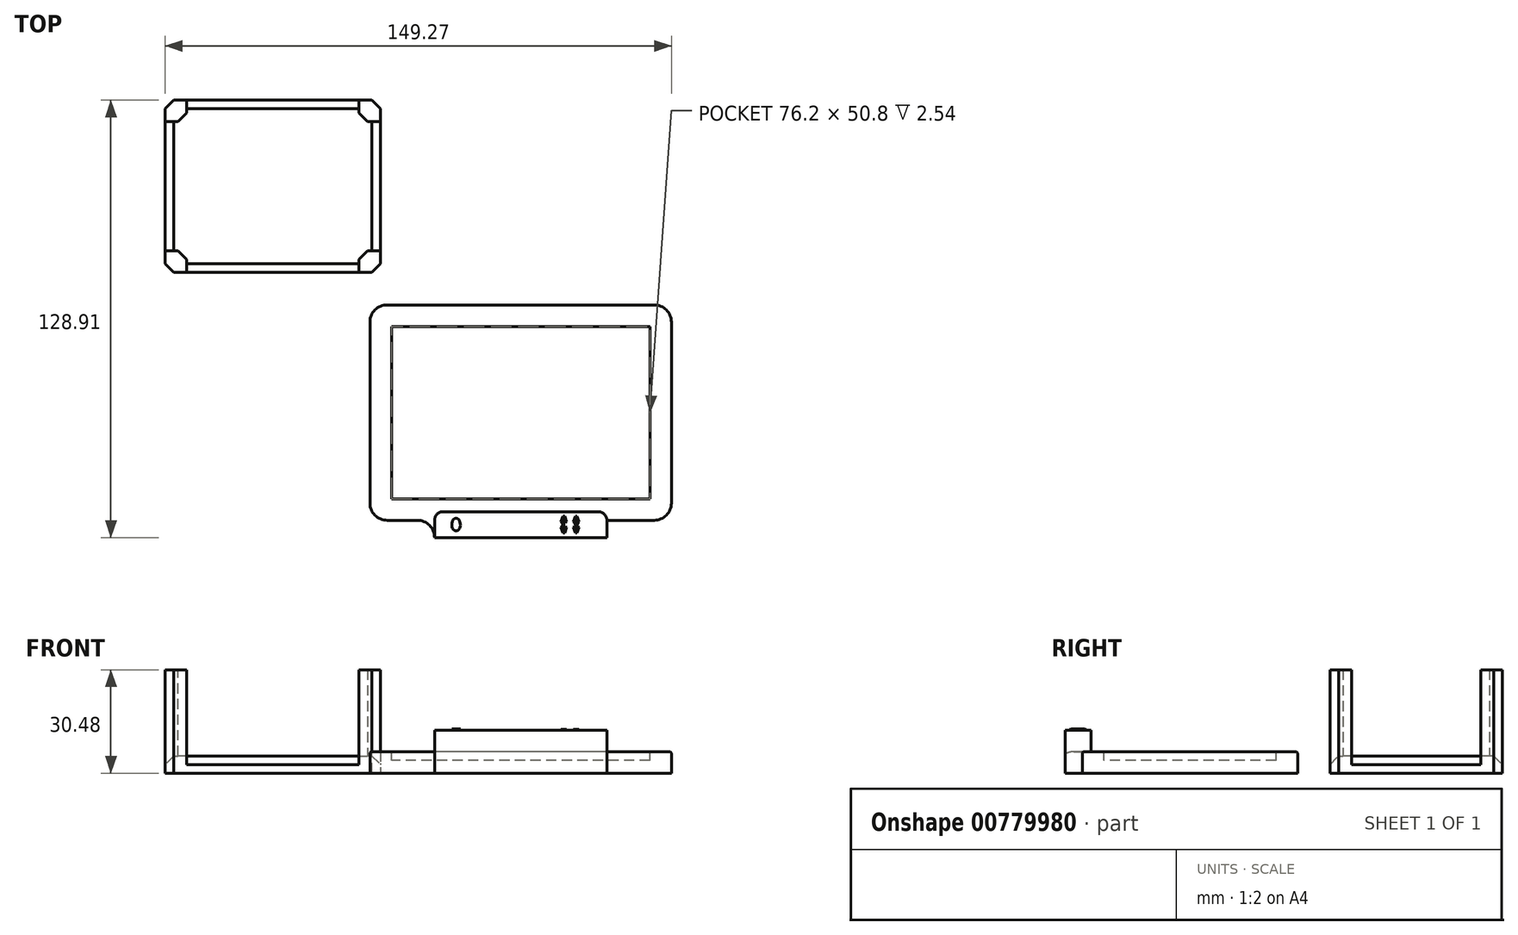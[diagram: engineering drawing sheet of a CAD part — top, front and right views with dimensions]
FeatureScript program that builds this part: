
annotation { "Feature Type Name" : "Feature", "Feature Type Description" : "" }
export const myFeature = defineFeature(function(context is Context, id is Id, definition is map)
    precondition{}
    {
        {
            var Q0;
            Q0=qCreatedBy(makeId("Top.planeOp"),FACE);
            var sketch = newSketch(context, id + "F0", { "sketchPlane" : qUnion([Q0])});
            skLineSegment(sketch, "E0.bottom", {"start": v(44.45, 31.75) * mm, "end": v(-44.45, 31.75) * mm});
            skLineSegment(sketch, "E0.top", {"start": v(44.45, -31.75) * mm, "end": v(-44.45, -31.75) * mm});
            skLineSegment(sketch, "E0.left", {"start": v(44.45, 31.75) * mm, "end": v(44.45, -31.75) * mm});
            skLineSegment(sketch, "E0.right", {"start": v(-44.45, 31.75) * mm, "end": v(-44.45, -31.75) * mm});
            skPoint(sketch, "E0.middle", {"position": v(0, 0) * mm});
            skSolve(sketch);
        }
        {
            var Q0;
            Q0 = qSketchRegion(id + "F0", true);
            extrude(context, id + "F1", {"entities" : qUnion([Q0]), "depth" : 6.35 * mm, "offsetDistance" : 25.4 * mm});
        }
        {
            var Q0;
            Q0=makeQuery(id+"F1.opExtrude","CAP_FACE",FACE,{"disambiguationData":[OSD([sQuery(id+"F0.wireOp",EDGE,"E0.bottom"),sQuery(id+"F0.wireOp",EDGE,"E0.top"),sQuery(id+"F0.wireOp",EDGE,"E0.left"),sQuery(id+"F0.wireOp",EDGE,"E0.right")])],"isStart":false});
            var sketch = newSketch(context, id + "F2", { "sketchPlane" : qUnion([Q0])});
            skLineSegment(sketch, "E1.bottom", {"start": v(44.45, 31.75) * mm, "end": v(-44.45, 31.75) * mm});
            skLineSegment(sketch, "E1.top", {"start": v(44.45, -31.75) * mm, "end": v(-44.45, -31.75) * mm});
            skLineSegment(sketch, "E1.left", {"start": v(44.45, 31.75) * mm, "end": v(44.45, -31.75) * mm});
            skLineSegment(sketch, "E1.right", {"start": v(-44.45, 31.75) * mm, "end": v(-44.45, -31.75) * mm});
            skPoint(sketch, "E1.middle", {"position": v(0, 0) * mm});
            skLineSegment(sketch, "E2.bottom", {"start": v(38.1, 25.4) * mm, "end": v(-38.1, 25.4) * mm});
            skLineSegment(sketch, "E2.top", {"start": v(38.1, -25.4) * mm, "end": v(-38.1, -25.4) * mm});
            skLineSegment(sketch, "E2.left", {"start": v(38.1, 25.4) * mm, "end": v(38.1, -25.4) * mm});
            skLineSegment(sketch, "E2.right", {"start": v(-38.1, 25.4) * mm, "end": v(-38.1, -25.4) * mm});
            skSolve(sketch);
        }
        {
            var Q0;
            Q0=makeQuery(id+"F2.imprint","IMPRINT",FACE,{"disambiguationData":[TD([[makeQuery(id+"F2.imprint","IMPRINT",EDGE,{"derivedFrom":sQuery(id+"F2.wireOp",EDGE,"E2.bottom")}),1.0]])]});
            extrude(context, id + "F3", {"entities" : qUnion([Q0]), "operationType" : NewBodyOperationType.REMOVE, "oppositeDirection" : true, "depth" : 2.54 * mm, "offsetDistance" : 25.4 * mm});
        }
        {
            var Q0;
            Q0=makeQuery(id+"F1.opExtrude","SWEPT_FACE",FACE,{"disambiguationData":[OSD([sQuery(id+"F0.wireOp",EDGE,"E0.top")])]});
            var sketch = newSketch(context, id + "F4", { "sketchPlane" : qUnion([Q0])});
            skLineSegment(sketch, "E3", {"start": v(0, 0) * mm, "end": v(0, 6.35) * mm});
            skLineSegment(sketch, "E4.bottom", {"start": v(25.4, 0) * mm, "end": v(-25.4, 0) * mm});
            skLineSegment(sketch, "E4.top", {"start": v(25.4, 12.7) * mm, "end": v(-25.4, 12.7) * mm});
            skLineSegment(sketch, "E4.left", {"start": v(25.4, 0) * mm, "end": v(25.4, 12.7) * mm});
            skLineSegment(sketch, "E4.right", {"start": v(-25.4, 0) * mm, "end": v(-25.4, 12.7) * mm});
            skPoint(sketch, "E4.middle", {"position": v(0, 6.35) * mm});
            skSolve(sketch);
        }
        {
            var Q0;
            Q0 = qSketchRegion(id + "F4", true);
            extrude(context, id + "F5", {"entities" : qUnion([Q0]), "operationType" : NewBodyOperationType.ADD, "depth" : 5.08 * mm, "offsetDistance" : 25.4 * mm});
        }
        {
            var Q0;
            Q0=makeQuery(id+"F5.opExtrude","CAP_FACE",FACE,{"disambiguationData":[OSD([sQuery(id+"F4.wireOp",EDGE,"E4.bottom"),sQuery(id+"F4.wireOp",EDGE,"E4.top"),sQuery(id+"F4.wireOp",EDGE,"E4.left"),sQuery(id+"F4.wireOp",EDGE,"E4.right")])],"isStart":true});
            extrude(context, id + "F6", {"entities" : qUnion([Q0]), "operationType" : NewBodyOperationType.ADD, "depth" : 2.54 * mm, "offsetDistance" : 25.4 * mm});
        }
        {
            var Q0;
            {var subQ0=sQuery(id+"F4.wireOp",EDGE,"E4.left");Q0=makeQuery(id+"F5.boolean.opBoolean","SPLIT",EDGE,{"disambiguationData":[topologyDisambiguationEdgeConnected([makeQuery(id+"F1.opExtrude","SWEPT_FACE",FACE,{"disambiguationData":[OSD([sQuery(id+"F0.wireOp",EDGE,"E0.top")])]})])],"derivedFrom":makeQuery(id+"F5.opExtrude","CAP_EDGE",EDGE,{"disambiguationData":[OSD([subQ0])],"isStart":true})});}
            var Q1;
            {var subQ0=sQuery(id+"F4.wireOp",EDGE,"E4.right");Q1=makeQuery(id+"F5.boolean.opBoolean","SPLIT",EDGE,{"disambiguationData":[topologyDisambiguationEdgeConnected([makeQuery(id+"F1.opExtrude","SWEPT_FACE",FACE,{"disambiguationData":[OSD([sQuery(id+"F0.wireOp",EDGE,"E0.top")])]})])],"derivedFrom":makeQuery(id+"F5.opExtrude","CAP_EDGE",EDGE,{"disambiguationData":[OSD([subQ0])],"isStart":true})});}
            var Q2;
            Q2=makeQuery(id+"F1.opExtrude","SWEPT_EDGE",EDGE,{"disambiguationData":[OSD([sQuery(id+"F0.wireOp",EDGE,"E0.bottom"),sQuery(id+"F0.wireOp",EDGE,"E0.left")])]});
            var Q3;
            Q3=makeQuery(id+"F1.opExtrude","SWEPT_EDGE",EDGE,{"disambiguationData":[OSD([sQuery(id+"F0.wireOp",EDGE,"E0.top"),sQuery(id+"F0.wireOp",EDGE,"E0.left")])]});
            var Q4;
            Q4=makeQuery(id+"F1.opExtrude","SWEPT_EDGE",EDGE,{"disambiguationData":[OSD([sQuery(id+"F0.wireOp",EDGE,"E0.top"),sQuery(id+"F0.wireOp",EDGE,"E0.right")])]});
            var Q5;
            Q5=makeQuery(id+"F1.opExtrude","SWEPT_EDGE",EDGE,{"disambiguationData":[OSD([sQuery(id+"F0.wireOp",EDGE,"E0.bottom"),sQuery(id+"F0.wireOp",EDGE,"E0.right")])]});
            fillet(context, id + "F7", {"entities" : qUnion([Q0, Q1, Q2, Q3, Q4, Q5]), "radius" : 5.08 * mm, "tangentPropagation" : true, "allowEdgeOverflow" : false});
        }
        {
            var Q0;
            Q0=makeQuery(id+"F6.opExtrude","CAP_EDGE",EDGE,{"disambiguationData":[OSD([sQuery(id+"F4.wireOp",EDGE,"E4.right")])],"isStart":false});
            var Q1;
            Q1=makeQuery(id+"F6.opExtrude","CAP_EDGE",EDGE,{"disambiguationData":[OSD([sQuery(id+"F4.wireOp",EDGE,"E4.left")])],"isStart":false});
            fillet(context, id + "F8", {"entities" : qUnion([Q0, Q1]), "radius" : 2.54 * mm, "tangentPropagation" : true, "allowEdgeOverflow" : false});
        }
        {
            var Q0;
            {var subQ0=sQuery(id+"F4.wireOp",EDGE,"E4.top");Q0=makeQuery(id+"F6.boolean.opBoolean","MERGE",FACE,{"derivedFrom":[makeQuery(id+"F5.opExtrude","SWEPT_FACE",FACE,{"disambiguationData":[OSD([subQ0])]}),makeQuery(id+"F6.opExtrude","SWEPT_FACE",FACE,{"disambiguationData":[OSD([subQ0])]})]});}
            var sketch = newSketch(context, id + "F9", { "sketchPlane" : qUnion([Q0])});
            skLineSegment(sketch, "E5", {"start": v(-25.4, -34.3) * mm, "end": v(-19.05, -34.3) * mm});
            skLineSegment(sketch, "E6", {"start": v(-19.05, -34.3) * mm, "end": v(-19.05, -33.02) * mm});
            skEllipse(sketch, "E7", {"center": v(-19.05, -33.02) * mm, "majorRadius": 1.9 * mm, "minorRadius": 1.27 * mm, "majorAxis": v(0, 1)});
            skSolve(sketch);
        }
        {
            var Q0;
            Q0 = qSketchRegion(id + "F9", true);
            extrude(context, id + "F10", {"entities" : qUnion([Q0]), "operationType" : NewBodyOperationType.ADD, "depth" : 0.38 * mm, "offsetDistance" : 25.4 * mm});
        }
        {
            var Q0;
            {var subQ0=sQuery(id+"F4.wireOp",EDGE,"E4.top");Q0=makeQuery(id+"F6.boolean.opBoolean","MERGE",FACE,{"derivedFrom":[makeQuery(id+"F5.opExtrude","SWEPT_FACE",FACE,{"disambiguationData":[OSD([subQ0])]}),makeQuery(id+"F6.opExtrude","SWEPT_FACE",FACE,{"disambiguationData":[OSD([subQ0])]})]});}
            var sketch = newSketch(context, id + "F11", { "sketchPlane" : qUnion([Q0])});
            skLineSegment(sketch, "E8.MirrorCS", {"start": v(12.95, -30.58) * mm, "end": v(13.56, -32.19) * mm});
            skLineSegment(sketch, "E9.MirrorCS", {"start": v(12.95, -30.58) * mm, "end": v(12.5, -30.58) * mm});
            skLineSegment(sketch, "E10.MirrorCS", {"start": v(12.5, -30.58) * mm, "end": v(11.9, -32.19) * mm});
            skLineSegment(sketch, "E11.MirrorCS", {"start": v(12.73, -30.8) * mm, "end": v(13.28, -32.47) * mm});
            skLineSegment(sketch, "E12.MirrorCS", {"start": v(12.5, -35.46) * mm, "end": v(11.9, -33.85) * mm});
            skLineSegment(sketch, "E13.MirrorCS", {"start": v(12.95, -35.46) * mm, "end": v(13.56, -33.85) * mm});
            skLineSegment(sketch, "E14.MirrorCS", {"start": v(12.95, -35.46) * mm, "end": v(12.5, -35.46) * mm});
            skLineSegment(sketch, "E15.MirrorCS", {"start": v(13.28, -33.57) * mm, "end": v(12.73, -35.24) * mm});
            skLineSegment(sketch, "E16.MirrorCS", {"start": v(12.17, -32.47) * mm, "end": v(11.9, -32.19) * mm});
            skLineSegment(sketch, "E17.MirrorCS", {"start": v(13.56, -32.19) * mm, "end": v(13.28, -32.47) * mm});
            skLineSegment(sketch, "E18.MirrorCS", {"start": v(13.28, -33.57) * mm, "end": v(13.56, -33.85) * mm});
            skLineSegment(sketch, "E19.bottom", {"start": v(13.28, -32.47) * mm, "end": v(12.17, -32.47) * mm});
            skLineSegment(sketch, "E19.top", {"start": v(13.28, -33.57) * mm, "end": v(12.17, -33.57) * mm});
            skLineSegment(sketch, "E19.left", {"start": v(13.28, -32.47) * mm, "end": v(13.28, -33.57) * mm});
            skLineSegment(sketch, "E19.right", {"start": v(12.17, -32.47) * mm, "end": v(12.17, -33.57) * mm});
            skPoint(sketch, "E19.middle", {"position": v(12.73, -33.02) * mm});
            skText(sketch, "E20", { "text": "C", "fontName": "OpenSans-Regular.ttf"});
            skLineSegment(sketch, "E21", {"start": v(12.17, -32.47) * mm, "end": v(12.73, -30.8) * mm});
            skLineSegment(sketch, "E22.MirrorCS", {"start": v(12.17, -33.57) * mm, "end": v(11.9, -33.85) * mm});
            skLineSegment(sketch, "E23", {"start": v(12.17, -33.57) * mm, "end": v(12.73, -35.24) * mm});
            skLineSegment(sketch, "E24", {"start": v(13.28, -33.02) * mm, "end": v(15.82, -33.02) * mm});
            skLineSegment(sketch, "E25", {"start": v(14.55, -33.02) * mm, "end": v(14.55, -32.47) * mm});
            skLineSegment(sketch, "E26.MirrorCS", {"start": v(16.38, -30.8) * mm, "end": v(15.82, -32.47) * mm});
            skLineSegment(sketch, "E27.MirrorCS", {"start": v(16.15, -30.58) * mm, "end": v(15.54, -32.19) * mm});
            skLineSegment(sketch, "E28.MirrorCS", {"start": v(16.93, -32.47) * mm, "end": v(16.38, -30.8) * mm});
            skLineSegment(sketch, "E29.MirrorCS", {"start": v(16.6, -30.58) * mm, "end": v(17.2, -32.19) * mm});
            skLineSegment(sketch, "E30.MirrorCS", {"start": v(16.15, -30.58) * mm, "end": v(16.6, -30.58) * mm});
            skLineSegment(sketch, "E31.MirrorCS", {"start": v(15.54, -32.19) * mm, "end": v(15.82, -32.47) * mm});
            skLineSegment(sketch, "E32.MirrorCS", {"start": v(16.93, -32.47) * mm, "end": v(17.2, -32.19) * mm});
            skLineSegment(sketch, "E33.MirrorCS", {"start": v(16.93, -33.57) * mm, "end": v(17.2, -33.85) * mm});
            skLineSegment(sketch, "E34.MirrorCS", {"start": v(16.93, -33.57) * mm, "end": v(16.38, -35.24) * mm});
            skLineSegment(sketch, "E35.MirrorCS", {"start": v(15.82, -33.57) * mm, "end": v(16.38, -35.24) * mm});
            skLineSegment(sketch, "E36.MirrorCS", {"start": v(16.15, -35.46) * mm, "end": v(15.54, -33.85) * mm});
            skLineSegment(sketch, "E37.MirrorCS", {"start": v(15.82, -33.57) * mm, "end": v(15.54, -33.85) * mm});
            skLineSegment(sketch, "E38.MirrorCS", {"start": v(16.15, -35.46) * mm, "end": v(16.6, -35.46) * mm});
            skLineSegment(sketch, "E39.MirrorCS", {"start": v(16.6, -35.46) * mm, "end": v(17.2, -33.85) * mm});
            const initialGuessF11  = {"E20": [0.01225, -0.03358, 1, 0, 0.00111]};
            skSetInitialGuess(sketch, initialGuessF11);
            skSolve(sketch);
        }
        {
            var Q0;
            Q0=makeQuery(id+"F11.imprint","IMPRINT",FACE,{"disambiguationData":[TD([[makeQuery(id+"F11.imprint","IMPRINT",EDGE,{"derivedFrom":sQuery(id+"F11.wireOp",EDGE,"E8.MirrorCS")}),-1.0]])]});
            var Q1;
            Q1=makeQuery(id+"F11.imprint","IMPRINT",FACE,{"disambiguationData":[TD([[makeQuery(id+"F11.imprint","IMPRINT",EDGE,{"derivedFrom":sQuery(id+"F11.wireOp",EDGE,"E12.MirrorCS")}),-1.0]])]});
            var Q2;
            Q2=makeQuery(id+"F11.imprint","IMPRINT",FACE,{"disambiguationData":[TD([[makeQuery(id+"F11.imprint","IMPRINT",EDGE,{"derivedFrom":sQuery(id+"F11.wireOp",EDGE,"E26.MirrorCS")}),-1.0]])]});
            var Q3;
            Q3=makeQuery(id+"F11.imprint","IMPRINT",FACE,{"disambiguationData":[TD([[makeQuery(id+"F11.imprint","IMPRINT",EDGE,{"derivedFrom":sQuery(id+"F11.wireOp",EDGE,"E33.MirrorCS")}),-1.0]])]});
            var Q4;
            Q4=makeQuery(id+"F11.imprint","IMPRINT",FACE,{"disambiguationData":[TD([[makeQuery(id+"F11.imprint","IMPRINT",EDGE,{"derivedFrom":sQuery(id+"F11.wireOp",EDGE,"E20.sketch_text.stroke-0")}),-1.0]])]});
            extrude(context, id + "F12", {"entities" : qUnion([Q0, Q1, Q2, Q3, Q4]), "operationType" : NewBodyOperationType.ADD, "depth" : 0.25 * mm, "offsetDistance" : 25.4 * mm});
        }
        {
            var Q0;
            {var subQ0=sQuery(id+"F4.wireOp",EDGE,"E4.top");Q0=makeQuery(id+"F6.boolean.opBoolean","MERGE",FACE,{"derivedFrom":[makeQuery(id+"F5.opExtrude","SWEPT_FACE",FACE,{"disambiguationData":[OSD([subQ0])]}),makeQuery(id+"F6.opExtrude","SWEPT_FACE",FACE,{"disambiguationData":[OSD([subQ0])]})]});}
            var sketch = newSketch(context, id + "F13", { "sketchPlane" : qUnion([Q0])});
            skLineSegment(sketch, "E40", {"start": v(15.82, -32.47) * mm, "end": v(15.97, -32.47) * mm});
            skLineSegment(sketch, "E41", {"start": v(15.97, -32.47) * mm, "end": v(15.97, -32.41) * mm});
            skLineSegment(sketch, "E42", {"start": v(16.99, -33.57) * mm, "end": v(16.93, -33.57) * mm});
            skText(sketch, "E43", { "text": "V\n", "fontName": "OpenSans-Regular.ttf"});
            const initialGuessF13  = {"E43": [0.01597, -0.03357, 1, 0, 0.0011]};
            skSetInitialGuess(sketch, initialGuessF13);
            skSolve(sketch);
        }
        {
            var Q0;
            Q0 = qSketchRegion(id + "F13", true);
            extrude(context, id + "F14", {"entities" : qUnion([Q0]), "operationType" : NewBodyOperationType.ADD, "depth" : 0.25 * mm, "offsetDistance" : 25.4 * mm});
        }
        {
            var Q0;
            Q0=makeQuery(id+"F1.opExtrude","CAP_EDGE",EDGE,{"disambiguationData":[OSD([sQuery(id+"F0.wireOp",EDGE,"E0.bottom")])],"isStart":false});
            var Q1;
            Q1=makeQuery(id+"F1.opExtrude","CAP_EDGE",EDGE,{"disambiguationData":[OSD([sQuery(id+"F0.wireOp",EDGE,"E0.right")])],"isStart":false});
            var Q2;
            Q2=makeQuery(id+"F1.opExtrude","CAP_EDGE",EDGE,{"disambiguationData":[OSD([sQuery(id+"F0.wireOp",EDGE,"E0.left")])],"isStart":false});
            var Q3;
            {var subQ0=sQuery(id+"F0.wireOp",EDGE,"E0.right");var subQ2=sQuery(id+"F0.wireOp",EDGE,"E0.top");var subQ3=makeQuery(id+"F1.opExtrude","SWEPT_FACE",FACE,{"disambiguationData":[OSD([subQ2])]});var subQ4=makeQuery(id+"F1.opExtrude","CAP_FACE",FACE,{"disambiguationData":[OSD([sQuery(id+"F0.wireOp",EDGE,"E0.bottom"),subQ2,sQuery(id+"F0.wireOp",EDGE,"E0.left"),subQ0])],"isStart":false});Q3=makeQuery(id+"F5.boolean.opBoolean","SPLIT",EDGE,{"disambiguationData":[topologyDisambiguationEdgeConnected([subQ4,subQ3]),TD([makeQuery(id+"F1.opExtrude","SWEPT_FACE",FACE,{"disambiguationData":[OSD([subQ0])]})])],"derivedFrom":makeQuery(id+"F1.opExtrude","CAP_EDGE",EDGE,{"disambiguationData":[OSD([subQ2])],"isStart":false})});}
            var Q4;
            {var subQ0=sQuery(id+"F0.wireOp",EDGE,"E0.left");var subQ2=sQuery(id+"F0.wireOp",EDGE,"E0.top");var subQ3=makeQuery(id+"F1.opExtrude","SWEPT_FACE",FACE,{"disambiguationData":[OSD([subQ2])]});var subQ4=makeQuery(id+"F1.opExtrude","CAP_FACE",FACE,{"disambiguationData":[OSD([sQuery(id+"F0.wireOp",EDGE,"E0.bottom"),subQ2,subQ0,sQuery(id+"F0.wireOp",EDGE,"E0.right")])],"isStart":false});Q4=makeQuery(id+"F5.boolean.opBoolean","SPLIT",EDGE,{"disambiguationData":[topologyDisambiguationEdgeConnected([subQ4,subQ3]),TD([makeQuery(id+"F1.opExtrude","SWEPT_FACE",FACE,{"disambiguationData":[OSD([subQ0])]})])],"derivedFrom":makeQuery(id+"F1.opExtrude","CAP_EDGE",EDGE,{"disambiguationData":[OSD([subQ2])],"isStart":false})});}
            var Q5;
            {var subQ0=sQuery(id+"F0.wireOp",EDGE,"E0.left");var subQ1=sQuery(id+"F0.wireOp",EDGE,"E0.top");Q5=makeQuery(id+"F7.opFillet","BLEND_EDGE",EDGE,{"blendedFrom":[makeQuery(id+"F1.opExtrude","SWEPT_EDGE",EDGE,{"disambiguationData":[OSD([subQ1,subQ0])]}),makeQuery(id+"F1.opExtrude","CAP_FACE",FACE,{"disambiguationData":[OSD([sQuery(id+"F0.wireOp",EDGE,"E0.bottom"),subQ1,subQ0,sQuery(id+"F0.wireOp",EDGE,"E0.right")])],"isStart":false})],"blendedInto":[makeQuery(id+"F1.opExtrude","CAP_FACE",FACE,{"disambiguationData":[OSD([sQuery(id+"F0.wireOp",EDGE,"E0.bottom"),subQ1,subQ0,sQuery(id+"F0.wireOp",EDGE,"E0.right")])],"isStart":false})]});}
            var Q6;
            {var subQ0=sQuery(id+"F0.wireOp",EDGE,"E0.left");var subQ1=sQuery(id+"F0.wireOp",EDGE,"E0.bottom");Q6=makeQuery(id+"F7.opFillet","BLEND_EDGE",EDGE,{"blendedFrom":[makeQuery(id+"F1.opExtrude","SWEPT_EDGE",EDGE,{"disambiguationData":[OSD([subQ1,subQ0])]}),makeQuery(id+"F1.opExtrude","CAP_FACE",FACE,{"disambiguationData":[OSD([subQ1,sQuery(id+"F0.wireOp",EDGE,"E0.top"),subQ0,sQuery(id+"F0.wireOp",EDGE,"E0.right")])],"isStart":false})],"blendedInto":[makeQuery(id+"F1.opExtrude","CAP_FACE",FACE,{"disambiguationData":[OSD([subQ1,sQuery(id+"F0.wireOp",EDGE,"E0.top"),subQ0,sQuery(id+"F0.wireOp",EDGE,"E0.right")])],"isStart":false})]});}
            var Q7;
            {var subQ0=sQuery(id+"F0.wireOp",EDGE,"E0.right");var subQ1=sQuery(id+"F0.wireOp",EDGE,"E0.bottom");Q7=makeQuery(id+"F7.opFillet","BLEND_EDGE",EDGE,{"blendedFrom":[makeQuery(id+"F1.opExtrude","SWEPT_EDGE",EDGE,{"disambiguationData":[OSD([subQ1,subQ0])]}),makeQuery(id+"F1.opExtrude","CAP_FACE",FACE,{"disambiguationData":[OSD([subQ1,sQuery(id+"F0.wireOp",EDGE,"E0.top"),sQuery(id+"F0.wireOp",EDGE,"E0.left"),subQ0])],"isStart":false})],"blendedInto":[makeQuery(id+"F1.opExtrude","CAP_FACE",FACE,{"disambiguationData":[OSD([subQ1,sQuery(id+"F0.wireOp",EDGE,"E0.top"),sQuery(id+"F0.wireOp",EDGE,"E0.left"),subQ0])],"isStart":false})]});}
            var Q8;
            {var subQ0=sQuery(id+"F0.wireOp",EDGE,"E0.right");var subQ1=sQuery(id+"F0.wireOp",EDGE,"E0.top");Q8=makeQuery(id+"F7.opFillet","BLEND_EDGE",EDGE,{"blendedFrom":[makeQuery(id+"F1.opExtrude","SWEPT_EDGE",EDGE,{"disambiguationData":[OSD([subQ1,subQ0])]}),makeQuery(id+"F1.opExtrude","CAP_FACE",FACE,{"disambiguationData":[OSD([sQuery(id+"F0.wireOp",EDGE,"E0.bottom"),subQ1,sQuery(id+"F0.wireOp",EDGE,"E0.left"),subQ0])],"isStart":false})],"blendedInto":[makeQuery(id+"F1.opExtrude","CAP_FACE",FACE,{"disambiguationData":[OSD([sQuery(id+"F0.wireOp",EDGE,"E0.bottom"),subQ1,sQuery(id+"F0.wireOp",EDGE,"E0.left"),subQ0])],"isStart":false})]});}
            fillet(context, id + "F15", {"entities" : qUnion([Q0, Q1, Q2, Q3, Q4, Q5, Q6, Q7, Q8]), "radius" : 0.64 * mm, "tangentPropagation" : true, "allowEdgeOverflow" : false});
        }
        {
            var Q0;
            Q0=qCreatedBy(makeId("Top.planeOp"),FACE);
            var sketch = newSketch(context, id + "F16", { "sketchPlane" : qUnion([Q0])});
            skLineSegment(sketch, "E44.bottom", {"start": v(-41.32, 41.28) * mm, "end": v(-104.82, 41.28) * mm});
            skLineSegment(sketch, "E44.top", {"start": v(-41.32, 92.08) * mm, "end": v(-104.82, 92.08) * mm});
            skLineSegment(sketch, "E44.left", {"start": v(-41.32, 41.28) * mm, "end": v(-41.32, 92.08) * mm});
            skLineSegment(sketch, "E44.right", {"start": v(-104.82, 41.28) * mm, "end": v(-104.82, 92.08) * mm});
            skPoint(sketch, "E44.middle", {"position": v(-73.07, 66.68) * mm});
            skSolve(sketch);
        }
        {
            var Q0;
            Q0 = qSketchRegion(id + "F16", true);
            extrude(context, id + "F17", {"entities" : qUnion([Q0]), "depth" : 5.08 * mm, "offsetDistance" : 25.4 * mm});
        }
        {
            var Q0;
            Q0=makeQuery(id+"F17.opExtrude","CAP_FACE",FACE,{"disambiguationData":[OSD([sQuery(id+"F16.wireOp",EDGE,"E44.bottom"),sQuery(id+"F16.wireOp",EDGE,"E44.top"),sQuery(id+"F16.wireOp",EDGE,"E44.left"),sQuery(id+"F16.wireOp",EDGE,"E44.right")])],"isStart":false});
            var sketch = newSketch(context, id + "F18", { "sketchPlane" : qUnion([Q0])});
            skLineSegment(sketch, "E45.bottom", {"start": v(-104.82, 92.08) * mm, "end": v(-98.47, 92.08) * mm});
            skLineSegment(sketch, "E45.top", {"start": v(-104.82, 85.73) * mm, "end": v(-98.47, 85.73) * mm});
            skLineSegment(sketch, "E45.left", {"start": v(-104.82, 92.08) * mm, "end": v(-104.82, 85.73) * mm});
            skLineSegment(sketch, "E45.right", {"start": v(-98.47, 92.08) * mm, "end": v(-98.47, 85.73) * mm});
            skLineSegment(sketch, "E46.bottom", {"start": v(-41.32, 92.08) * mm, "end": v(-47.67, 92.08) * mm});
            skLineSegment(sketch, "E46.top", {"start": v(-41.32, 85.73) * mm, "end": v(-47.67, 85.73) * mm});
            skLineSegment(sketch, "E46.left", {"start": v(-41.32, 92.08) * mm, "end": v(-41.32, 85.73) * mm});
            skLineSegment(sketch, "E46.right", {"start": v(-47.67, 92.08) * mm, "end": v(-47.67, 85.73) * mm});
            skLineSegment(sketch, "E47.bottom", {"start": v(-41.32, 41.28) * mm, "end": v(-47.67, 41.28) * mm});
            skLineSegment(sketch, "E47.top", {"start": v(-41.32, 47.63) * mm, "end": v(-47.67, 47.63) * mm});
            skLineSegment(sketch, "E47.left", {"start": v(-41.32, 41.28) * mm, "end": v(-41.32, 47.63) * mm});
            skLineSegment(sketch, "E47.right", {"start": v(-47.67, 41.28) * mm, "end": v(-47.67, 47.63) * mm});
            skLineSegment(sketch, "E48.bottom", {"start": v(-104.82, 41.28) * mm, "end": v(-98.47, 41.28) * mm});
            skLineSegment(sketch, "E48.top", {"start": v(-104.82, 47.63) * mm, "end": v(-98.47, 47.63) * mm});
            skLineSegment(sketch, "E48.left", {"start": v(-104.82, 41.28) * mm, "end": v(-104.82, 47.63) * mm});
            skLineSegment(sketch, "E48.right", {"start": v(-98.47, 41.28) * mm, "end": v(-98.47, 47.63) * mm});
            skSolve(sketch);
        }
        {
            var Q0;
            Q0 = qSketchRegion(id + "F18", true);
            extrude(context, id + "F19", {"entities" : qUnion([Q0]), "operationType" : NewBodyOperationType.ADD, "depth" : 25.4 * mm, "offsetDistance" : 25.4 * mm});
        }
        {
            var Q0;
            Q0=makeQuery(id+"F19.boolean.opBoolean","MERGE",EDGE,{"derivedFrom":[makeQuery(id+"F17.opExtrude","SWEPT_EDGE",EDGE,{"disambiguationData":[OSD([sQuery(id+"F16.wireOp",EDGE,"E44.bottom"),sQuery(id+"F16.wireOp",EDGE,"E44.left")])]}),makeQuery(id+"F19.opExtrude","SWEPT_EDGE",EDGE,{"disambiguationData":[OSD([sQuery(id+"F18.wireOp",EDGE,"E47.bottom"),sQuery(id+"F18.wireOp",EDGE,"E47.left")])]})]});
            var Q1;
            Q1=makeQuery(id+"F19.boolean.opBoolean","MERGE",EDGE,{"derivedFrom":[makeQuery(id+"F17.opExtrude","SWEPT_EDGE",EDGE,{"disambiguationData":[OSD([sQuery(id+"F16.wireOp",EDGE,"E44.top"),sQuery(id+"F16.wireOp",EDGE,"E44.left")])]}),makeQuery(id+"F19.opExtrude","SWEPT_EDGE",EDGE,{"disambiguationData":[OSD([sQuery(id+"F18.wireOp",EDGE,"E46.bottom"),sQuery(id+"F18.wireOp",EDGE,"E46.left")])]})]});
            var Q2;
            Q2=makeQuery(id+"F19.boolean.opBoolean","MERGE",EDGE,{"derivedFrom":[makeQuery(id+"F17.opExtrude","SWEPT_EDGE",EDGE,{"disambiguationData":[OSD([sQuery(id+"F16.wireOp",EDGE,"E44.bottom"),sQuery(id+"F16.wireOp",EDGE,"E44.right")])]}),makeQuery(id+"F19.opExtrude","SWEPT_EDGE",EDGE,{"disambiguationData":[OSD([sQuery(id+"F18.wireOp",EDGE,"E48.bottom"),sQuery(id+"F18.wireOp",EDGE,"E48.left")])]})]});
            var Q3;
            Q3=makeQuery(id+"F19.boolean.opBoolean","MERGE",EDGE,{"derivedFrom":[makeQuery(id+"F17.opExtrude","SWEPT_EDGE",EDGE,{"disambiguationData":[OSD([sQuery(id+"F16.wireOp",EDGE,"E44.top"),sQuery(id+"F16.wireOp",EDGE,"E44.right")])]}),makeQuery(id+"F19.opExtrude","SWEPT_EDGE",EDGE,{"disambiguationData":[OSD([sQuery(id+"F18.wireOp",EDGE,"E45.bottom"),sQuery(id+"F18.wireOp",EDGE,"E45.left")])]})]});
            var Q4;
            Q4=makeQuery(id+"F17.opExtrude","CAP_EDGE",EDGE,{"disambiguationData":[OSD([sQuery(id+"F16.wireOp",EDGE,"E44.top")])],"isStart":false});
            var Q5;
            Q5=makeQuery(id+"F17.opExtrude","CAP_EDGE",EDGE,{"disambiguationData":[OSD([sQuery(id+"F16.wireOp",EDGE,"E44.left")])],"isStart":false});
            var Q6;
            Q6=makeQuery(id+"F17.opExtrude","CAP_EDGE",EDGE,{"disambiguationData":[OSD([sQuery(id+"F16.wireOp",EDGE,"E44.bottom")])],"isStart":false});
            var Q7;
            Q7=makeQuery(id+"F17.opExtrude","CAP_EDGE",EDGE,{"disambiguationData":[OSD([sQuery(id+"F16.wireOp",EDGE,"E44.right")])],"isStart":false});
            var Q8;
            Q8=makeQuery(id+"F19.opExtrude","SWEPT_EDGE",EDGE,{"disambiguationData":[OSD([sQuery(id+"F18.wireOp",EDGE,"E48.top"),sQuery(id+"F18.wireOp",EDGE,"E48.right")])]});
            var Q9;
            Q9=makeQuery(id+"F19.opExtrude","SWEPT_EDGE",EDGE,{"disambiguationData":[OSD([sQuery(id+"F18.wireOp",EDGE,"E45.top"),sQuery(id+"F18.wireOp",EDGE,"E45.right")])]});
            var Q10;
            Q10=makeQuery(id+"F19.opExtrude","SWEPT_EDGE",EDGE,{"disambiguationData":[OSD([sQuery(id+"F18.wireOp",EDGE,"E46.top"),sQuery(id+"F18.wireOp",EDGE,"E46.right")])]});
            var Q11;
            Q11=makeQuery(id+"F19.opExtrude","SWEPT_EDGE",EDGE,{"disambiguationData":[OSD([sQuery(id+"F18.wireOp",EDGE,"E47.top"),sQuery(id+"F18.wireOp",EDGE,"E47.right")])]});
            chamfer(context, id + "F20", {"entities" : qUnion([Q0, Q1, Q2, Q3, Q4, Q5, Q6, Q7, Q8, Q9, Q10, Q11]), "width" : 2.54 * mm, "tangentPropagation" : true});
        }
    });
